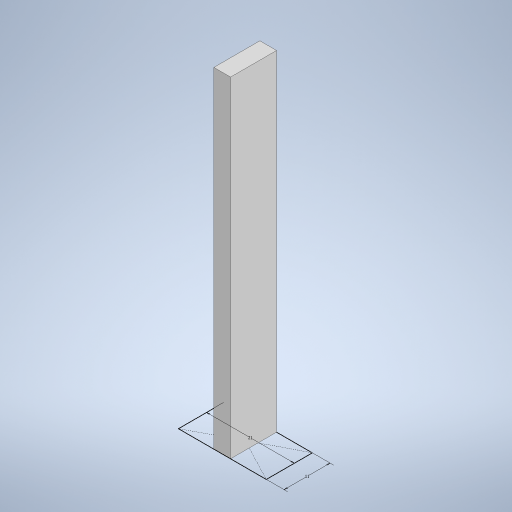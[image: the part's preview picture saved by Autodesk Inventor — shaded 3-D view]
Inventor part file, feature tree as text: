
AUTODESK INVENTOR PART (.ipt)
format: ipt  version: 2024 (Build 280153000, 153)  size: 233,984 bytes
history: native  units: mm
features: sketch x2, extrude x1
ambient origin geometry x8: Origin, YZ Plane, XZ Plane, XY Plane, X Axis, Y Axis, Z Axis, Center Point
bodies: Body1 (feature_tree)
feature tree (3):
  extrude  "돌출3"  Depth=11.0mm
  sketch  "스케치5"
  sketch  "스케치4"
